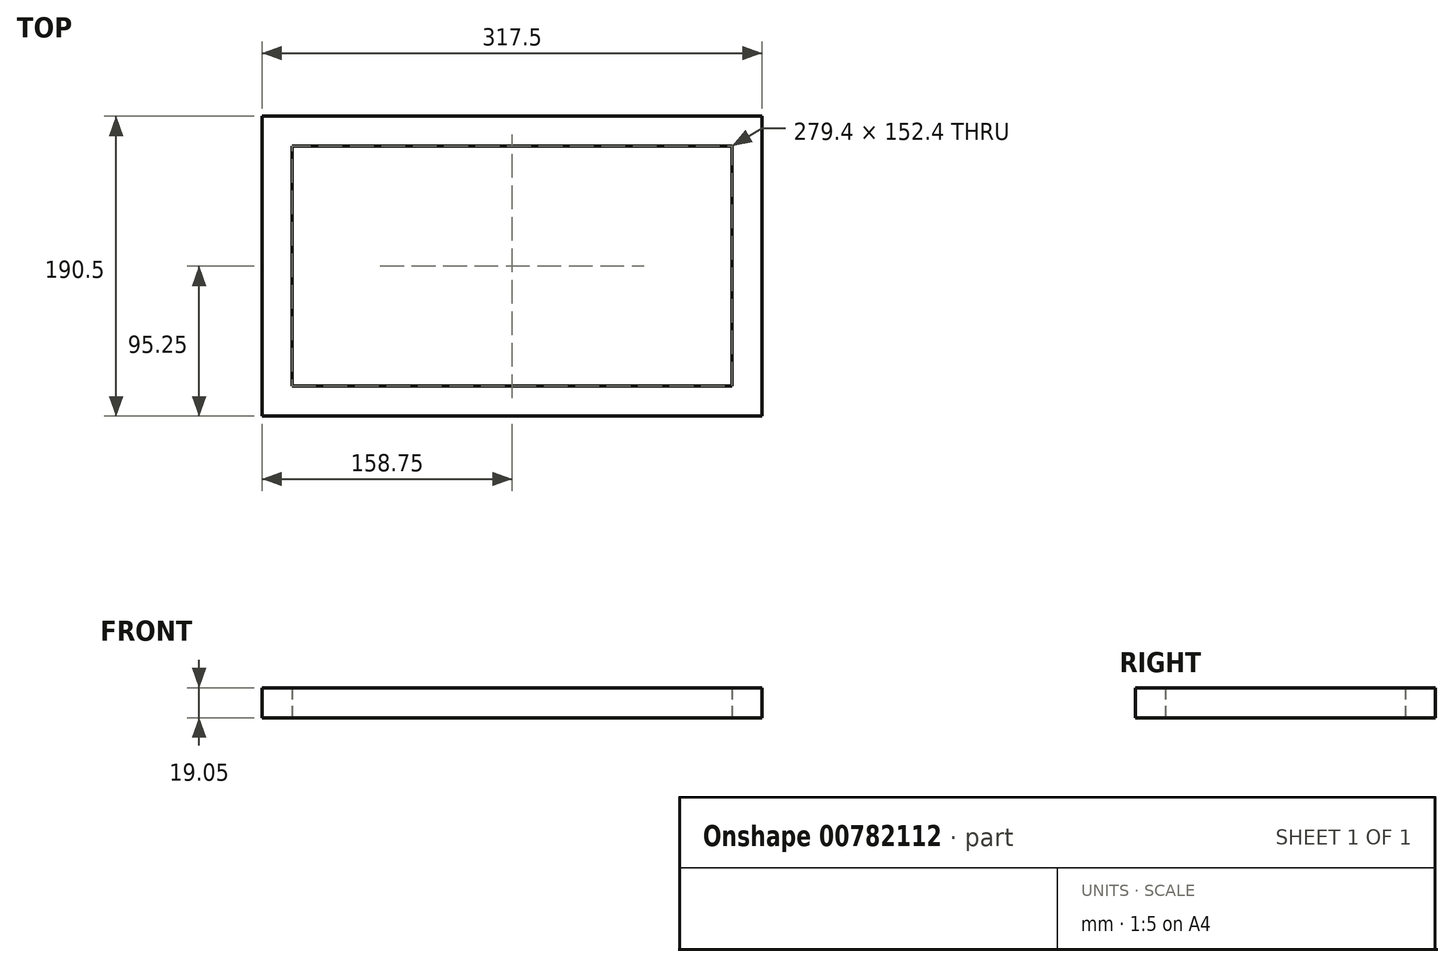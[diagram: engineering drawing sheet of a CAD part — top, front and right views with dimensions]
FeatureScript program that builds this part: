
annotation { "Feature Type Name" : "Feature", "Feature Type Description" : "" }
export const myFeature = defineFeature(function(context is Context, id is Id, definition is map)
    precondition{}
    {
        {
            var Q0;
            Q0=qCreatedBy(makeId("Top.planeOp"),FACE);
            var sketch = newSketch(context, id + "F0", { "sketchPlane" : qUnion([Q0])});
            skLineSegment(sketch, "E0.bottom", {"start": v(139.7, 76.2) * mm, "end": v(-139.7, 76.2) * mm});
            skLineSegment(sketch, "E0.top", {"start": v(139.7, -76.2) * mm, "end": v(-139.7, -76.2) * mm});
            skLineSegment(sketch, "E0.left", {"start": v(139.7, 76.2) * mm, "end": v(139.7, -76.2) * mm});
            skLineSegment(sketch, "E0.right", {"start": v(-139.7, 76.2) * mm, "end": v(-139.7, -76.2) * mm});
            skPoint(sketch, "E0.middle", {"position": v(0, 0) * mm});
            skLineSegment(sketch, "E1.0", {"start": v(158.75, 95.25) * mm, "end": v(-158.75, 95.25) * mm});
            skLineSegment(sketch, "E1.1", {"start": v(158.75, 95.25) * mm, "end": v(158.75, -95.25) * mm});
            skLineSegment(sketch, "E1.2", {"start": v(158.75, -95.25) * mm, "end": v(-158.75, -95.25) * mm});
            skLineSegment(sketch, "E1.3", {"start": v(-158.75, 95.25) * mm, "end": v(-158.75, -95.25) * mm});
            skSolve(sketch);
        }
        {
            var Q0;
            Q0 = qSketchRegion(id + "F0", true);
            extrude(context, id + "F1", {"entities" : qUnion([Q0]), "depth" : 19.05 * mm, "offsetDistance" : 25.4 * mm});
        }
    });
